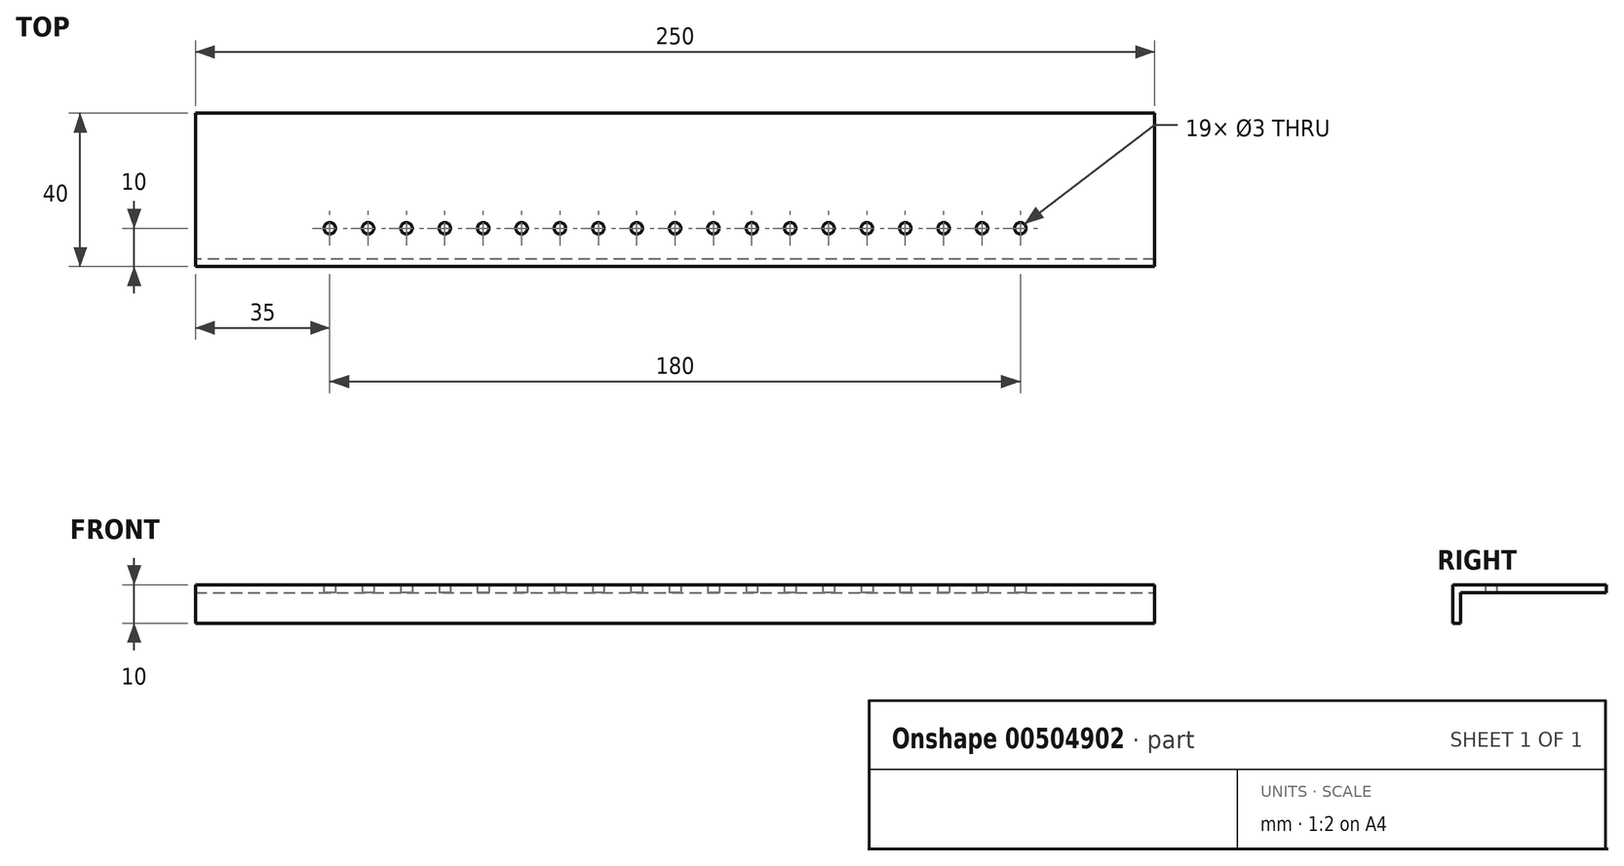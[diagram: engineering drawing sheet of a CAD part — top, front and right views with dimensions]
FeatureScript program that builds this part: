
annotation { "Feature Type Name" : "Feature", "Feature Type Description" : "" }
export const myFeature = defineFeature(function(context is Context, id is Id, definition is map)
    precondition{}
    {
        {
            var Q0;
            Q0=qCreatedBy(makeId("Top.planeOp"),FACE);
            var sketch = newSketch(context, id + "F0", { "sketchPlane" : qUnion([Q0])});
            skLineSegment(sketch, "E0.bottom", {"start": v(-125, 30) * mm, "end": v(125, 30) * mm});
            skLineSegment(sketch, "E0.top", {"start": v(-125, -10) * mm, "end": v(125, -10) * mm});
            skLineSegment(sketch, "E0.left", {"start": v(-125, 30) * mm, "end": v(-125, -10) * mm});
            skLineSegment(sketch, "E0.right", {"start": v(125, 30) * mm, "end": v(125, -10) * mm});
            skCircle(sketch, "E1", {"center": v(0, 0) * mm, "radius": 1.5 * mm});
            skCircle(sketch, "E2.1.0.0", {"center": v(10, 0) * mm, "radius": 1.5 * mm});
            skCircle(sketch, "E2.2.0.0", {"center": v(20, 0) * mm, "radius": 1.5 * mm});
            skCircle(sketch, "E2.3.0.0", {"center": v(30, 0) * mm, "radius": 1.5 * mm});
            skCircle(sketch, "E2.4.0.0", {"center": v(40, 0) * mm, "radius": 1.5 * mm});
            skLineSegment(sketch, "E2.direction1", {"start": v(0, 0) * mm, "end": v(10, 0) * mm, "construction": true});
            skCircle(sketch, "E3.1.0.0", {"center": v(-10, 0) * mm, "radius": 1.5 * mm});
            skCircle(sketch, "E3.2.0.0", {"center": v(-20, 0) * mm, "radius": 1.5 * mm});
            skLineSegment(sketch, "E3.direction1", {"start": v(0, 0) * mm, "end": v(-10, 0) * mm, "construction": true});
            skCircle(sketch, "E4.0.3.0", {"center": v(-30, 0) * mm, "radius": 1.5 * mm});
            skCircle(sketch, "E4.0.4.0", {"center": v(-40, 0) * mm, "radius": 1.5 * mm});
            skPoint(sketch, "E5", {"position": v(0, 30) * mm});
            skCircle(sketch, "E6.0.5.0", {"center": v(50, 0) * mm, "radius": 1.5 * mm});
            skCircle(sketch, "E6.0.6.0", {"center": v(60, 0) * mm, "radius": 1.5 * mm});
            skCircle(sketch, "E6.0.7.0", {"center": v(70, 0) * mm, "radius": 1.5 * mm});
            skCircle(sketch, "E6.0.8.0", {"center": v(80, 0) * mm, "radius": 1.5 * mm});
            skCircle(sketch, "E6.0.9.0", {"center": v(90, 0) * mm, "radius": 1.5 * mm});
            skCircle(sketch, "E7.0.5.0", {"center": v(-50, 0) * mm, "radius": 1.5 * mm});
            skCircle(sketch, "E7.0.6.0", {"center": v(-60, 0) * mm, "radius": 1.5 * mm});
            skCircle(sketch, "E7.0.7.0", {"center": v(-70, 0) * mm, "radius": 1.5 * mm});
            skCircle(sketch, "E7.0.8.0", {"center": v(-80, 0) * mm, "radius": 1.5 * mm});
            skCircle(sketch, "E7.0.9.0", {"center": v(-90, 0) * mm, "radius": 1.5 * mm});
            skSolve(sketch);
        }
        {
            var Q0;
            Q0=makeQuery(id+"F0.imprint","IMPRINT",FACE,{"disambiguationData":[TD([[makeQuery(id+"F0.imprint","IMPRINT",EDGE,{"derivedFrom":sQuery(id+"F0.wireOp",EDGE,"E0.bottom")}),-1.0]])]});
            extrude(context, id + "F1", {"entities" : qUnion([Q0]), "depth" : 2 * mm});
        }
        {
            var Q0;
            Q0=makeQuery(id+"F1.opExtrude","CAP_FACE",FACE,{"disambiguationData":[OSD([sQuery(id+"F0.wireOp",EDGE,"E0.bottom"),sQuery(id+"F0.wireOp",EDGE,"E0.top"),sQuery(id+"F0.wireOp",EDGE,"E0.left"),sQuery(id+"F0.wireOp",EDGE,"E0.right"),sQuery(id+"F0.wireOp",EDGE,"E1"),sQuery(id+"F0.wireOp",EDGE,"E2.1.0.0"),sQuery(id+"F0.wireOp",EDGE,"E2.2.0.0"),sQuery(id+"F0.wireOp",EDGE,"E2.3.0.0"),sQuery(id+"F0.wireOp",EDGE,"E2.4.0.0"),sQuery(id+"F0.wireOp",EDGE,"E3.1.0.0"),sQuery(id+"F0.wireOp",EDGE,"E3.2.0.0"),sQuery(id+"F0.wireOp",EDGE,"E4.0.3.0"),sQuery(id+"F0.wireOp",EDGE,"E4.0.4.0"),sQuery(id+"F0.wireOp",EDGE,"E6.0.5.0"),sQuery(id+"F0.wireOp",EDGE,"E6.0.6.0"),sQuery(id+"F0.wireOp",EDGE,"E6.0.7.0"),sQuery(id+"F0.wireOp",EDGE,"E6.0.8.0"),sQuery(id+"F0.wireOp",EDGE,"E6.0.9.0"),sQuery(id+"F0.wireOp",EDGE,"E7.0.5.0"),sQuery(id+"F0.wireOp",EDGE,"E7.0.6.0"),sQuery(id+"F0.wireOp",EDGE,"E7.0.7.0"),sQuery(id+"F0.wireOp",EDGE,"E7.0.8.0"),sQuery(id+"F0.wireOp",EDGE,"E7.0.9.0")])],"isStart":true});
            var sketch = newSketch(context, id + "F2", { "sketchPlane" : qUnion([Q0])});
            skLineSegment(sketch, "E8.bottom", {"start": v(125, 10) * mm, "end": v(-125, 10) * mm});
            skLineSegment(sketch, "E8.top", {"start": v(125, 8) * mm, "end": v(-125, 8) * mm});
            skLineSegment(sketch, "E8.left", {"start": v(125, 10) * mm, "end": v(125, 8) * mm});
            skLineSegment(sketch, "E8.right", {"start": v(-125, 10) * mm, "end": v(-125, 8) * mm});
            skSolve(sketch);
        }
        {
            var Q0;
            Q0=makeQuery(id+"F2.imprint","IMPRINT",FACE,{"disambiguationData":[TD([[makeQuery(id+"F2.imprint","IMPRINT",EDGE,{"derivedFrom":sQuery(id+"F2.wireOp",EDGE,"E8.bottom")}),-1.0]])]});
            extrude(context, id + "F3", {"entities" : qUnion([Q0]), "operationType" : NewBodyOperationType.ADD, "depth" : 8 * mm});
        }
    });
